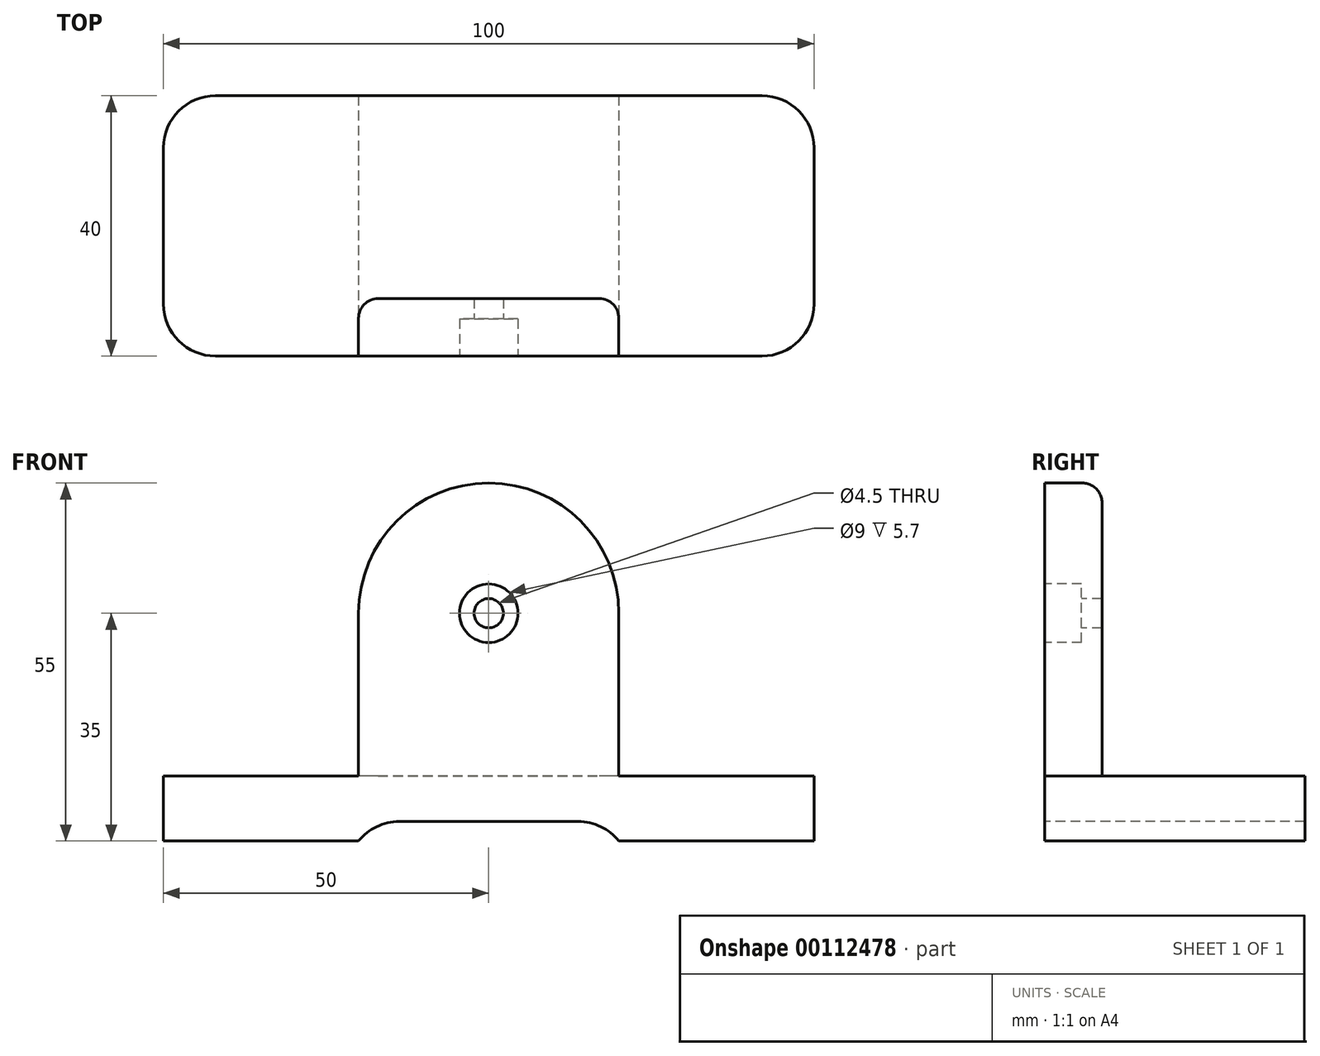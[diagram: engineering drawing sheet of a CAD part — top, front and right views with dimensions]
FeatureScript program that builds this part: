
annotation { "Feature Type Name" : "Feature", "Feature Type Description" : "" }
export const myFeature = defineFeature(function(context is Context, id is Id, definition is map)
    precondition{}
    {
        {
            var Q0;
            Q0=qCreatedBy(makeId("Top.planeOp"),FACE);
            var sketch = newSketch(context, id + "F0", { "sketchPlane" : qUnion([Q0])});
            skLineSegment(sketch, "E0.bottom", {"start": v(0, 0) * mm, "end": v(-100, 0) * mm});
            skLineSegment(sketch, "E0.top", {"start": v(0, 40) * mm, "end": v(-100, 40) * mm});
            skLineSegment(sketch, "E0.left", {"start": v(0, 0) * mm, "end": v(0, 40) * mm});
            skLineSegment(sketch, "E0.right", {"start": v(-100, 0) * mm, "end": v(-100, 40) * mm});
            skSolve(sketch);
        }
        {
            var Q0;
            Q0 = qSketchRegion(id + "F0", true);
            extrude(context, id + "F1", {"entities" : qUnion([Q0]), "depth" : 10 * mm});
        }
        {
            var Q0;
            Q0=makeQuery(id+"F1.opExtrude","SWEPT_FACE",FACE,{"disambiguationData":[OSD([sQuery(id+"F0.wireOp",EDGE,"E0.bottom")])]});
            var sketch = newSketch(context, id + "F2", { "sketchPlane" : qUnion([Q0])});
            skLineSegment(sketch, "E1", {"start": v(-70, 35) * mm, "end": v(-70, 0) * mm});
            skLineSegment(sketch, "E2", {"start": v(-70, 0) * mm, "end": v(-30, 0) * mm});
            skLineSegment(sketch, "E3", {"start": v(-30, 0) * mm, "end": v(-30, 35) * mm});
            skArc(sketch, "E4", {"start": v(-70, 35) * mm, "mid": v(-50, 55) * mm, "end": v(-30, 35) * mm});
            skSolve(sketch);
        }
        {
            var Q0;
            Q0 = qSketchRegion(id + "F2", true);
            extrude(context, id + "F3", {"entities" : qUnion([Q0]), "operationType" : NewBodyOperationType.ADD, "oppositeDirection" : true, "depth" : 8.83 * mm});
        }
        {
            var Q0;
            Q0=qCreatedBy(makeId("Front.planeOp"),FACE);
            var sketch = newSketch(context, id + "F4", { "sketchPlane" : qUnion([Q0])});
            skLineSegment(sketch, "E5.bottom", {"start": v(-30, 0) * mm, "end": v(-70, 0) * mm});
            skLineSegment(sketch, "E5.top", {"start": v(-30, 3) * mm, "end": v(-70, 3) * mm});
            skLineSegment(sketch, "E5.left", {"start": v(-30, 0) * mm, "end": v(-30, 3) * mm});
            skLineSegment(sketch, "E5.right", {"start": v(-70, 0) * mm, "end": v(-70, 3) * mm});
            skSolve(sketch);
        }
        {
            var Q0;
            Q0 = qSketchRegion(id + "F4", true);
            extrude(context, id + "F5", {"entities" : qUnion([Q0]), "operationType" : NewBodyOperationType.REMOVE, "endBound" : BoundingType.THROUGH_ALL, "oppositeDirection" : true, "depth" : 25 * mm});
        }
        {
            var Q0;
            Q0=makeQuery(id+"F3.boolean.opBoolean","MERGE",FACE,{"derivedFrom":[makeQuery(id+"F1.opExtrude","SWEPT_FACE",FACE,{"disambiguationData":[OSD([sQuery(id+"F0.wireOp",EDGE,"E0.bottom")])]}),makeQuery(id+"F3.opExtrude","CAP_FACE",FACE,{"disambiguationData":[OSD([sQuery(id+"F2.wireOp",EDGE,"E1"),sQuery(id+"F2.wireOp",EDGE,"E2"),sQuery(id+"F2.wireOp",EDGE,"E3"),sQuery(id+"F2.wireOp",EDGE,"E4")])],"isStart":true})]});
            var sketch = newSketch(context, id + "F6", { "sketchPlane" : qUnion([Q0])});
            skCircle(sketch, "E6", {"center": v(-50, 35) * mm, "radius": 2.25 * mm});
            skSolve(sketch);
        }
        {
            var Q0;
            Q0 = qSketchRegion(id + "F6", true);
            extrude(context, id + "F7", {"entities" : qUnion([Q0]), "operationType" : NewBodyOperationType.REMOVE, "endBound" : BoundingType.THROUGH_ALL, "oppositeDirection" : true, "depth" : 5.7 * mm});
        }
        {
            var Q0;
            Q0=makeQuery(id+"F3.boolean.opBoolean","MERGE",FACE,{"derivedFrom":[makeQuery(id+"F1.opExtrude","SWEPT_FACE",FACE,{"disambiguationData":[OSD([sQuery(id+"F0.wireOp",EDGE,"E0.bottom")])]}),makeQuery(id+"F3.opExtrude","CAP_FACE",FACE,{"disambiguationData":[OSD([sQuery(id+"F2.wireOp",EDGE,"E1"),sQuery(id+"F2.wireOp",EDGE,"E2"),sQuery(id+"F2.wireOp",EDGE,"E3"),sQuery(id+"F2.wireOp",EDGE,"E4")])],"isStart":true})]});
            var sketch = newSketch(context, id + "F8", { "sketchPlane" : qUnion([Q0])});
            skCircle(sketch, "E7", {"center": v(-50, 35) * mm, "radius": 4.5 * mm});
            skSolve(sketch);
        }
        {
            var Q0;
            Q0 = qSketchRegion(id + "F8", true);
            extrude(context, id + "F9", {"entities" : qUnion([Q0]), "operationType" : NewBodyOperationType.REMOVE, "oppositeDirection" : true, "depth" : 5.7 * mm});
        }
        {
            var Q0;
            Q0=makeQuery(id+"F5.boolean.opBoolean","COPY",EDGE,{"derivedFrom":makeQuery(id+"F5.opExtrude","SWEPT_EDGE",EDGE,{"disambiguationData":[OSD([sQuery(id+"F4.wireOp",EDGE,"E5.top"),sQuery(id+"F4.wireOp",EDGE,"E5.left")])]})});
            var Q1;
            Q1=makeQuery(id+"F1.opExtrude","SWEPT_EDGE",EDGE,{"disambiguationData":[OSD([sQuery(id+"F0.wireOp",EDGE,"E0.bottom"),sQuery(id+"F0.wireOp",EDGE,"E0.right")])]});
            var Q2;
            Q2=makeQuery(id+"F1.opExtrude","SWEPT_EDGE",EDGE,{"disambiguationData":[OSD([sQuery(id+"F0.wireOp",EDGE,"E0.top"),sQuery(id+"F0.wireOp",EDGE,"E0.right")])]});
            var Q3;
            Q3=makeQuery(id+"F1.opExtrude","SWEPT_EDGE",EDGE,{"disambiguationData":[OSD([sQuery(id+"F0.wireOp",EDGE,"E0.top"),sQuery(id+"F0.wireOp",EDGE,"E0.left")])]});
            var Q4;
            Q4=makeQuery(id+"F1.opExtrude","SWEPT_EDGE",EDGE,{"disambiguationData":[OSD([sQuery(id+"F0.wireOp",EDGE,"E0.bottom"),sQuery(id+"F0.wireOp",EDGE,"E0.left")])]});
            fillet(context, id + "F10", {"entities" : qUnion([Q0, Q1, Q2, Q3, Q4]), "radius" : 8 * mm, "tangentPropagation" : true, "allowEdgeOverflow" : false});
        }
        {
            var Q0;
            Q0=makeQuery(id+"F5.boolean.opBoolean","COPY",EDGE,{"derivedFrom":makeQuery(id+"F5.opExtrude","SWEPT_EDGE",EDGE,{"disambiguationData":[OSD([sQuery(id+"F4.wireOp",EDGE,"E5.top"),sQuery(id+"F4.wireOp",EDGE,"E5.right")])]})});
            fillet(context, id + "F11", {"entities" : qUnion([Q0]), "radius" : 8 * mm, "tangentPropagation" : true, "allowEdgeOverflow" : false});
        }
        {
            var Q0;
            Q0=makeQuery(id+"F3.opExtrude","CAP_EDGE",EDGE,{"disambiguationData":[OSD([sQuery(id+"F2.wireOp",EDGE,"E4")])],"isStart":false});
            fillet(context, id + "F12", {"entities" : qUnion([Q0]), "radius" : 3 * mm, "tangentPropagation" : true, "allowEdgeOverflow" : false});
        }
    });
